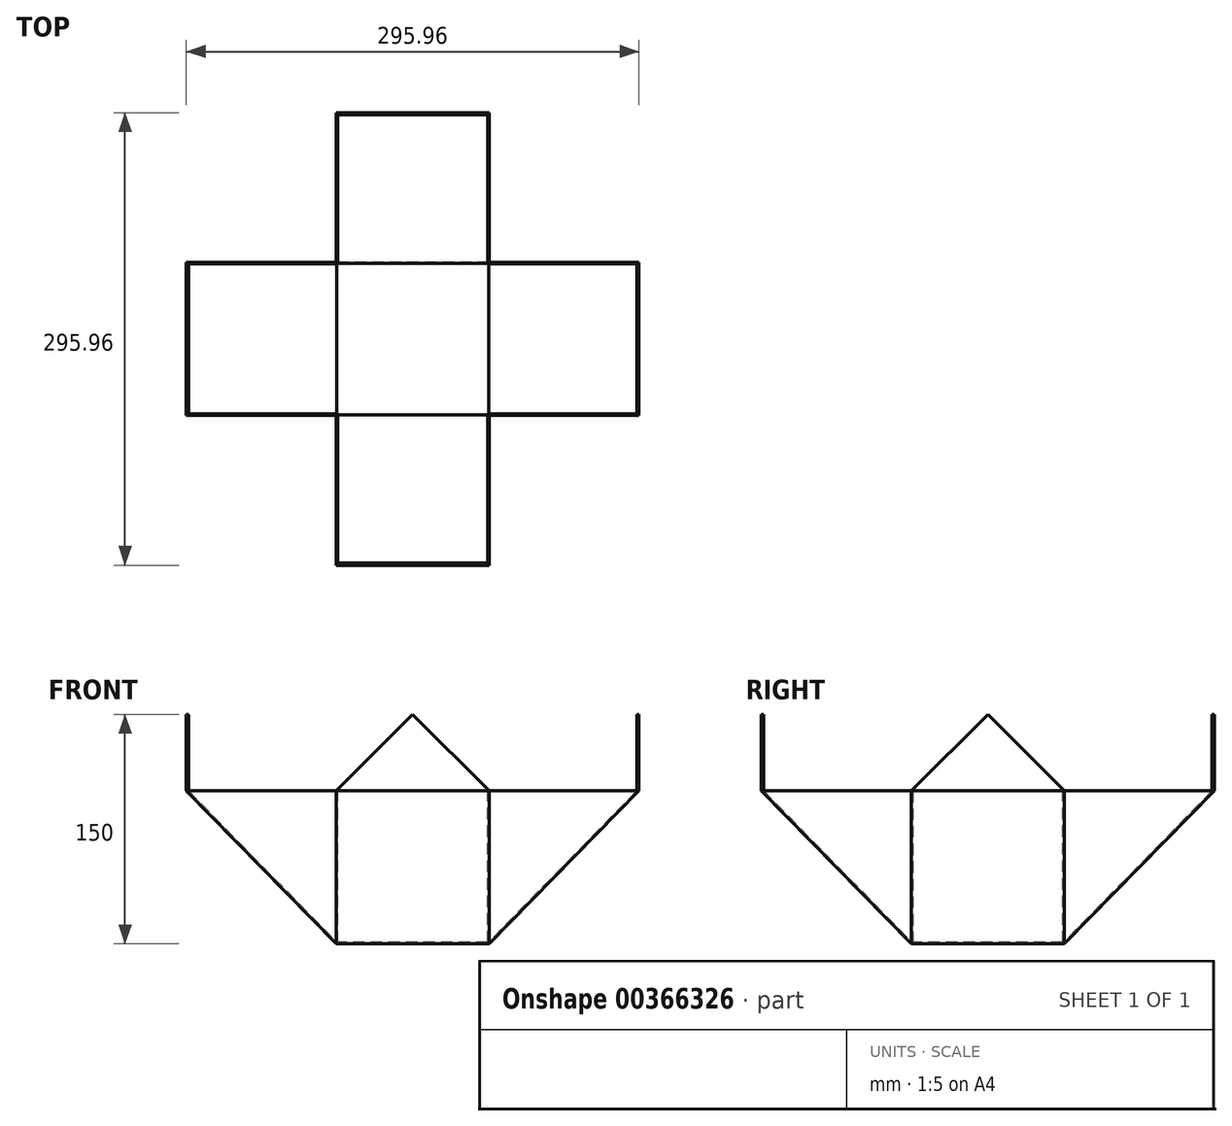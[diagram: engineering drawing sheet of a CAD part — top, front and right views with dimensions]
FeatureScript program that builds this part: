
annotation { "Feature Type Name" : "Feature", "Feature Type Description" : "" }
export const myFeature = defineFeature(function(context is Context, id is Id, definition is map)
    precondition{}
    {
        {
            var Q0;
            Q0=qCreatedBy(makeId("Top.planeOp"),FACE);
            var sketch = newSketch(context, id + "F0", { "sketchPlane" : qUnion([Q0])});
            skLineSegment(sketch, "E0.bottom", {"start": v(50, 50) * mm, "end": v(-50, 50) * mm});
            skLineSegment(sketch, "E0.top", {"start": v(50, -50) * mm, "end": v(-50, -50) * mm});
            skLineSegment(sketch, "E0.left", {"start": v(50, 50) * mm, "end": v(50, -50) * mm});
            skLineSegment(sketch, "E0.right", {"start": v(-50, 50) * mm, "end": v(-50, -50) * mm});
            skPoint(sketch, "E0.middle", {"position": v(0, 0) * mm});
            skSolve(sketch);
        }
        {
            var Q0;
            Q0 = qSketchRegion(id + "F0", true);
            extrude(context, id + "F1", {"entities" : qUnion([Q0]), "depth" : 100 * mm});
        }
        {
            var Q0;
            Q0=makeQuery(id+"F1.opExtrude","SWEPT_FACE",FACE,{"disambiguationData":[OSD([sQuery(id+"F0.wireOp",EDGE,"E0.top")])]});
            var sketch = newSketch(context, id + "F2", { "sketchPlane" : qUnion([Q0])});
            skCircle(sketch, "E1", {"center": v(50, 0) * mm, "radius": 140 * mm, "construction": true});
            skLineSegment(sketch, "E2", {"start": v(50, 100) * mm, "end": v(147.98, 100) * mm});
            skLineSegment(sketch, "E3", {"start": v(147.98, 100) * mm, "end": v(50, 0) * mm});
            skCircle(sketch, "E4", {"center": v(-50, 0) * mm, "radius": 140 * mm, "construction": true});
            skLineSegment(sketch, "E5", {"start": v(-50, 100) * mm, "end": v(-147.98, 100) * mm});
            skLineSegment(sketch, "E6", {"start": v(-147.98, 100) * mm, "end": v(-50, 0) * mm});
            skSolve(sketch);
        }
        {
            var Q0;
            Q0=makeQuery(id+"F2.imprint","IMPRINT",FACE,{"disambiguationData":[TD([[makeQuery(id+"F2.imprint","IMPRINT",EDGE,{"derivedFrom":sQuery(id+"F2.wireOp",EDGE,"E5")}),1.0]])]});
            var Q1;
            Q1=makeQuery(id+"F2.imprint","IMPRINT",FACE,{"disambiguationData":[TD([[makeQuery(id+"F2.imprint","IMPRINT",EDGE,{"derivedFrom":sQuery(id+"F2.wireOp",EDGE,"E2")}),-1.0]])]});
            extrude(context, id + "F3", {"entities" : qUnion([Q0, Q1]), "operationType" : NewBodyOperationType.ADD, "oppositeDirection" : true, "depth" : 100 * mm});
        }
        {
            var Q0;
            Q0=qCreatedBy(makeId("Front.planeOp"),FACE);
            var sketch = newSketch(context, id + "F4", { "sketchPlane" : qUnion([Q0])});
            skLineSegment(sketch, "E7", {"start": v(0, 0) * mm, "end": v(0, 185.15) * mm, "construction": true});
            skSolve(sketch);
        }
        {
            var Q0;
            Q0=makeQuery(id+"F1.opExtrude","SWEPT_BODY",BODY,{"disambiguationData":[OSD([sQuery(id+"F0.wireOp",EDGE,"E0.bottom"),sQuery(id+"F0.wireOp",EDGE,"E0.top"),sQuery(id+"F0.wireOp",EDGE,"E0.left"),sQuery(id+"F0.wireOp",EDGE,"E0.right")])]});
            var Q1;
            Q1=sQuery(id+"F4.wireOp",EDGE,"E7");
            circularPattern(context, id + "F5", {"operationType" : NewBodyOperationType.ADD, "entities" : qUnion([Q0]), "axis" : qUnion([Q1]), "angle" : 90 * degree, "instanceCount" : 2, "equalSpace" : true});
        }
        {
            var Q0;
            {var subQ0=makeQuery(id+"F3.boolean.opBoolean","MERGE",FACE,{"derivedFrom":[makeQuery(id+"F1.opExtrude","CAP_FACE",FACE,{"disambiguationData":[OSD([sQuery(id+"F0.wireOp",EDGE,"E0.bottom"),sQuery(id+"F0.wireOp",EDGE,"E0.top"),sQuery(id+"F0.wireOp",EDGE,"E0.left"),sQuery(id+"F0.wireOp",EDGE,"E0.right")])],"isStart":false}),makeQuery(id+"F3.opExtrude","SWEPT_FACE",FACE,{"disambiguationData":[OSD([sQuery(id+"F2.wireOp",EDGE,"E2")])]}),makeQuery(id+"F3.opExtrude","SWEPT_FACE",FACE,{"disambiguationData":[OSD([sQuery(id+"F2.wireOp",EDGE,"E5")])]})]});Q0=makeQuery(id+"F5.boolean.opBoolean","MERGE",FACE,{"derivedFrom":[subQ0,makeQuery(id+"F5.opPattern","COPY",FACE,{"derivedFrom":subQ0,"instanceName":"1"})]});}
            shell(context, id + "F6", {"entities" : qUnion([Q0]), "thickness" : 1 * mm});
        }
        {
            var Q0;
            {var subQ0=makeQuery(id+"F3.boolean.opBoolean","MERGE",FACE,{"derivedFrom":[makeQuery(id+"F1.opExtrude","CAP_FACE",FACE,{"disambiguationData":[OSD([sQuery(id+"F0.wireOp",EDGE,"E0.bottom"),sQuery(id+"F0.wireOp",EDGE,"E0.top"),sQuery(id+"F0.wireOp",EDGE,"E0.left"),sQuery(id+"F0.wireOp",EDGE,"E0.right")])],"isStart":false}),makeQuery(id+"F3.opExtrude","SWEPT_FACE",FACE,{"disambiguationData":[OSD([sQuery(id+"F2.wireOp",EDGE,"E2")])]}),makeQuery(id+"F3.opExtrude","SWEPT_FACE",FACE,{"disambiguationData":[OSD([sQuery(id+"F2.wireOp",EDGE,"E5")])]})]});Q0=makeQuery(id+"F5.boolean.opBoolean","MERGE",FACE,{"derivedFrom":[subQ0,makeQuery(id+"F5.opPattern","COPY",FACE,{"derivedFrom":subQ0,"instanceName":"1"})]});}
            var sketch = newSketch(context, id + "F7", { "sketchPlane" : qUnion([Q0])});
            skLineSegment(sketch, "E8.bottom", {"start": v(-147.98, 50) * mm, "end": v(-146.58, 50) * mm});
            skLineSegment(sketch, "E8.top", {"start": v(-147.98, -50) * mm, "end": v(-146.58, -50) * mm});
            skLineSegment(sketch, "E8.left", {"start": v(-147.98, 50) * mm, "end": v(-147.98, -50) * mm});
            skLineSegment(sketch, "E8.right", {"start": v(-146.58, 50) * mm, "end": v(-146.58, -50) * mm});
            skSolve(sketch);
        }
        {
            var Q0;
            Q0 = qSketchRegion(id + "F7", true);
            extrude(context, id + "F8", {"entities" : qUnion([Q0]), "operationType" : NewBodyOperationType.ADD, "depth" : 100 * mm});
        }
        {
            var Q0;
            Q0=makeQuery(id+"F8.opExtrude","SWEPT_FACE",FACE,{"disambiguationData":[OSD([sQuery(id+"F7.wireOp",EDGE,"E8.left")])]});
            var sketch = newSketch(context, id + "F9", { "sketchPlane" : qUnion([Q0])});
            skLineSegment(sketch, "E9", {"start": v(0, 200) * mm, "end": v(0, 100) * mm, "construction": true});
            skLineSegment(sketch, "E10", {"start": v(-50, 100) * mm, "end": v(0, 150) * mm});
            skLineSegment(sketch, "E11", {"start": v(0, 150) * mm, "end": v(50, 100) * mm});
            skSolve(sketch);
        }
        {
            var Q0;
            Q0=makeQuery(id+"F9.imprint","IMPRINT",FACE,{"disambiguationData":[TD([[makeQuery(id+"F9.imprint","IMPRINT",EDGE,{"derivedFrom":sQuery(id+"F9.wireOp",EDGE,"E10")}),1.0]])]});
            extrude(context, id + "F10", {"entities" : qUnion([Q0]), "operationType" : NewBodyOperationType.REMOVE, "oppositeDirection" : true, "depth" : 2 * mm});
        }
        {
            var Q0;
            Q0=makeQuery(id+"F1.opExtrude","SWEPT_BODY",BODY,{"disambiguationData":[OSD([sQuery(id+"F0.wireOp",EDGE,"E0.bottom"),sQuery(id+"F0.wireOp",EDGE,"E0.top"),sQuery(id+"F0.wireOp",EDGE,"E0.left"),sQuery(id+"F0.wireOp",EDGE,"E0.right")])]});
            var Q1;
            Q1=sQuery(id+"F4.wireOp",EDGE,"E7");
            circularPattern(context, id + "F11", {"operationType" : NewBodyOperationType.ADD, "entities" : qUnion([Q0]), "axis" : qUnion([Q1]), "angle" : 360 * degree, "instanceCount" : 4, "equalSpace" : true});
        }
    });
